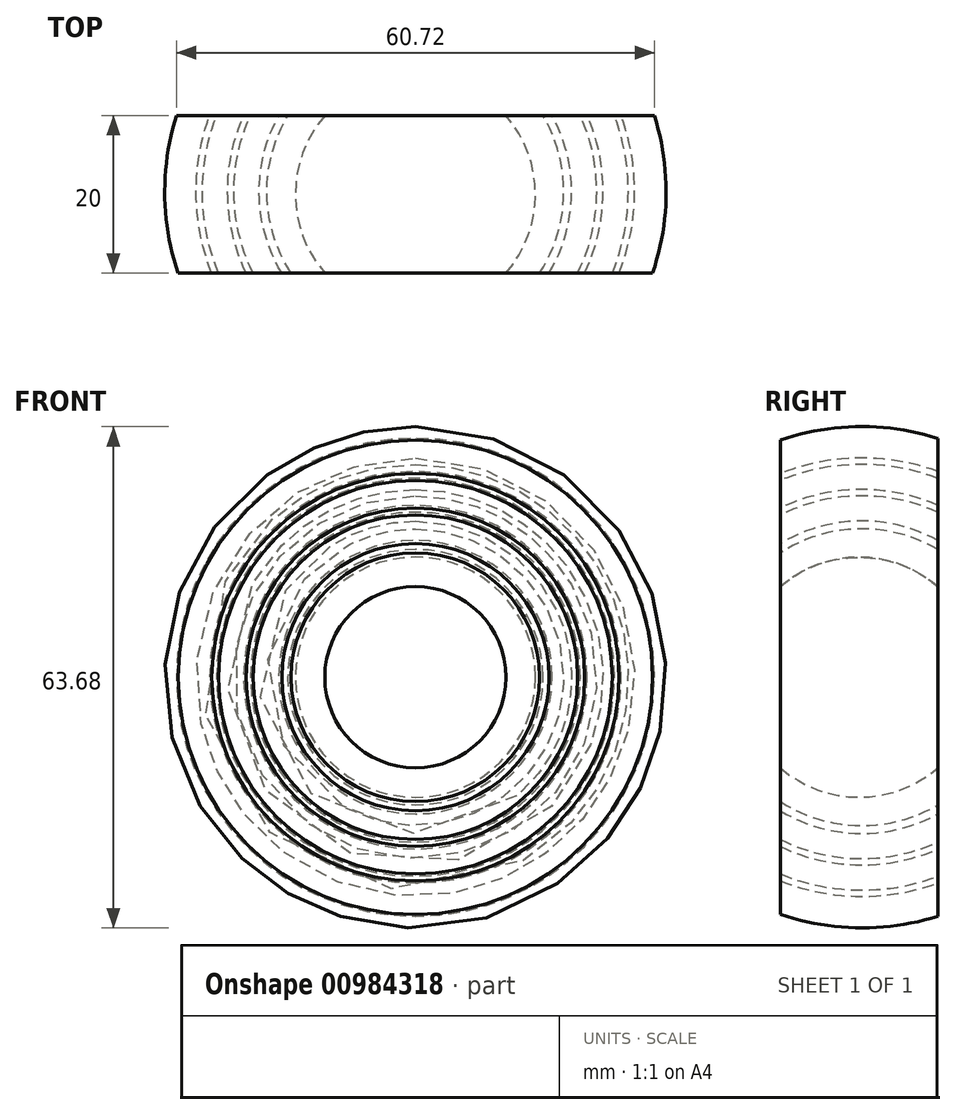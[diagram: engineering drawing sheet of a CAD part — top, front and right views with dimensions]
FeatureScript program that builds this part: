
annotation { "Feature Type Name" : "Feature", "Feature Type Description" : "" }
export const myFeature = defineFeature(function(context is Context, id is Id, definition is map)
    precondition{}
    {
        {
            var Q0;
            Q0=qCreatedBy(makeId("Top.planeOp"),FACE);
            var sketch = newSketch(context, id + "F0", { "sketchPlane" : qUnion([Q0])});
            skArc(sketch, "E0", {"start": v(-11.5, 10) * mm, "mid": v(-15.24, 0) * mm, "end": v(-11.5, -10) * mm});
            skArc(sketch, "E1.0", {"start": v(-17.37, 10) * mm, "mid": v(-19.84, -0.05) * mm, "end": v(-16.97, -10) * mm});
            skArc(sketch, "E2.0", {"start": v(-21.82, 10) * mm, "mid": v(-23.84, -0.03) * mm, "end": v(-21.5, -10) * mm});
            skArc(sketch, "E3.0", {"start": v(-20.94, 10) * mm, "mid": v(-23.04, -0.04) * mm, "end": v(-20.61, -10) * mm});
            skArc(sketch, "E4.0", {"start": v(-16.22, 10) * mm, "mid": v(-18.84, -0.06) * mm, "end": v(-15.79, -10) * mm});
            skArc(sketch, "E5.0", {"start": v(-26.13, 10) * mm, "mid": v(-27.84, -0.02) * mm, "end": v(-25.87, -10) * mm});
            skArc(sketch, "E6.0", {"start": v(-25.28, 10) * mm, "mid": v(-27.04, -0.03) * mm, "end": v(-25, -10) * mm});
            skArc(sketch, "E7.0", {"start": v(-30.36, 10) * mm, "mid": v(-31.84, -0.02) * mm, "end": v(-30.13, -10) * mm});
            skLineSegment(sketch, "E8", {"start": v(-30.36, 10) * mm, "end": v(-26.13, 10) * mm});
            skLineSegment(sketch, "E9.MirrorCS", {"start": v(-30.36, -10) * mm, "end": v(-25.87, -10) * mm});
            skLineSegment(sketch, "E10.trimOffspring", {"start": v(16.04, 10) * mm, "end": v(17.22, 10) * mm});
            skLineSegment(sketch, "E11.trimOffspring", {"start": v(-16.22, 10) * mm, "end": v(-11.5, 10) * mm});
            skLineSegment(sketch, "E12.trimOffspring", {"start": v(-20.94, 10) * mm, "end": v(-17.37, 10) * mm});
            skLineSegment(sketch, "E13.trimOffspring", {"start": v(-25.28, 10) * mm, "end": v(-21.82, 10) * mm});
            skLineSegment(sketch, "E14.trimOffspring", {"start": v(-25, -10) * mm, "end": v(-21.5, -10) * mm});
            skLineSegment(sketch, "E15.trimOffspring", {"start": v(-20.61, -10) * mm, "end": v(-16.97, -10) * mm});
            skLineSegment(sketch, "E16.trimOffspring", {"start": v(-15.79, -10) * mm, "end": v(-11.5, -10) * mm});
            skLineSegment(sketch, "E17.trimOffspring", {"start": v(26.27, -10) * mm, "end": v(30.76, -10) * mm});
            skPoint(sketch, "E18.trimOffspring.end.orphan", {"position": v(30.76, 10) * mm});
            skLineSegment(sketch, "E19", {"start": v(0, 9.7) * mm, "end": v(0, -10.3) * mm});
            skSolve(sketch);
        }
        {
            var Q0;
            {var subQ0=sQuery(id+"F0.wireOp",EDGE,"E5.0");Q0=makeQuery(id+"F0.imprint","IMPRINT",FACE,{"disambiguationData":[TD([[makeQuery(id+"F0.imprint","IMPRINT",EDGE,{"derivedFrom":subQ0}),-1.0]])]});}
            var Q1;
            Q1=makeQuery(id+"F0.imprint","IMPRINT",FACE,{"disambiguationData":[TD([[makeQuery(id+"F0.imprint","IMPRINT",EDGE,{"derivedFrom":sQuery(id+"F0.wireOp",EDGE,"E2.0")}),-1.0]])]});
            var Q2;
            Q2=makeQuery(id+"F0.imprint","IMPRINT",FACE,{"disambiguationData":[TD([[makeQuery(id+"F0.imprint","IMPRINT",EDGE,{"derivedFrom":sQuery(id+"F0.wireOp",EDGE,"E1.0")}),-1.0]])]});
            var Q3;
            Q3=makeQuery(id+"F0.imprint","IMPRINT",FACE,{"disambiguationData":[TD([[makeQuery(id+"F0.imprint","IMPRINT",EDGE,{"derivedFrom":sQuery(id+"F0.wireOp",EDGE,"E0")}),-1.0]])]});
            var Q4;
            Q4=sQuery(id+"F0.wireOp",EDGE,"E19");
            revolve(context, id + "F1", {"surfaceOperationType" : NewSurfaceOperationType.NEW, "entities" : qUnion([Q0, Q1, Q2, Q3]), "axis" : qUnion([Q4]), "revolveType" : RevolveType.FULL});
        }
    });
